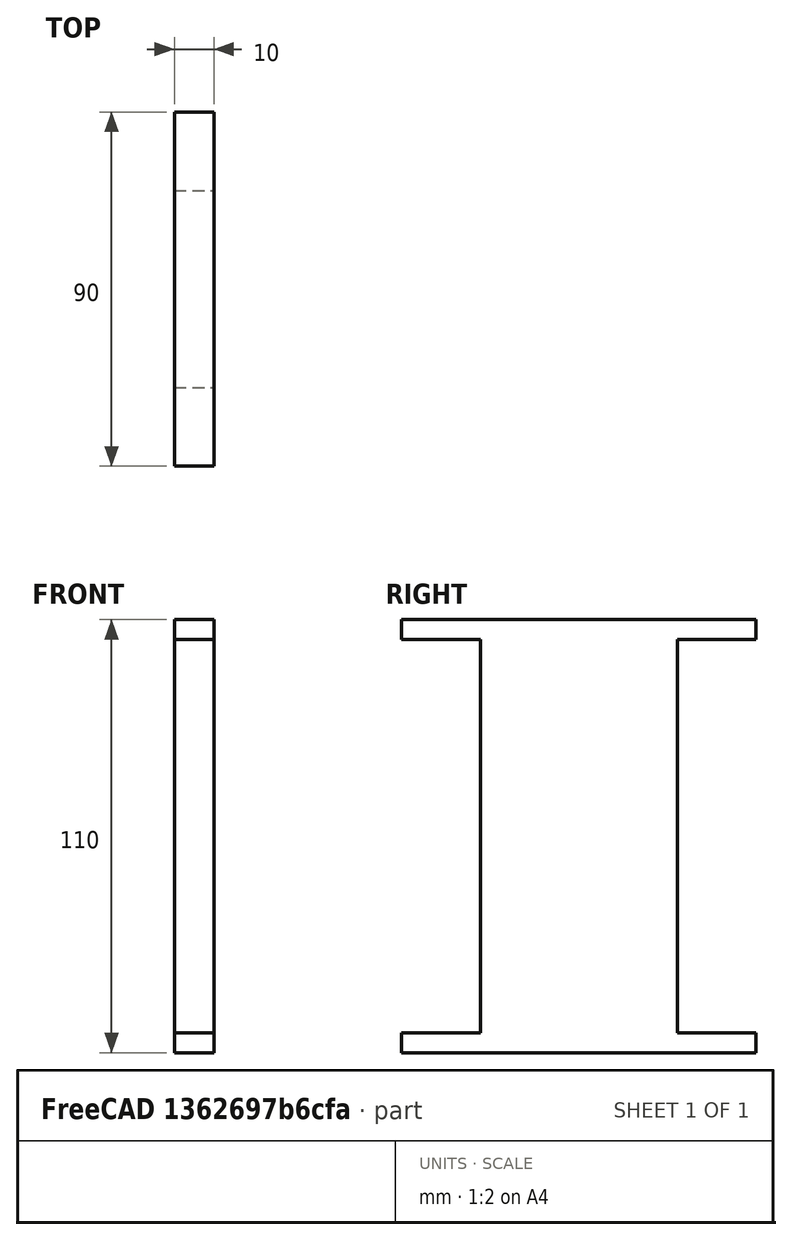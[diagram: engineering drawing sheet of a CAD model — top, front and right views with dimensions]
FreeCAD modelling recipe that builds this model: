
FCSTD DOCUMENT  (FreeCAD 0.20R29603 (Git))
Label: ws
License: All rights reserved
LicenseURL: http://en.wikipedia.org/wiki/All_rights_reserved
objects: Sketcher::SketchObject×1, PartDesign::Pad×1, PartDesign::Body×1
note: 4 computed .brp shape members not serialized (recipe doc carries the construction recipe); baked Part::Feature solids carry a one-line shape summary decoded from their .brp

FEATURE [Sketcher::SketchObject] Sketch
  FullyConstrained = true
  MapMode = 5
  Placement = pos=(0,0,0) rot=(0.57735,0.57735,0.57735;2.0944rad)
  Support = -> [YZ_Plane]
  sketch-geometry (12):
    g0: LineSegment StartX=-45 StartY=55 StartZ=0 EndX=45 EndY=55 EndZ=0
    g1: LineSegment StartX=45 StartY=55 StartZ=0 EndX=45 EndY=50 EndZ=0
    g2: LineSegment StartX=45 StartY=50 StartZ=0 EndX=25 EndY=50 EndZ=0
    g3: LineSegment StartX=25 StartY=50 StartZ=0 EndX=25 EndY=-50 EndZ=0
    g4: LineSegment StartX=25 StartY=-50 StartZ=0 EndX=45 EndY=-50 EndZ=0
    g5: LineSegment StartX=45 StartY=-50 StartZ=0 EndX=45 EndY=-55 EndZ=0
    g6: LineSegment StartX=45 StartY=-55 StartZ=0 EndX=-45 EndY=-55 EndZ=0
    g7: LineSegment StartX=-45 StartY=-55 StartZ=0 EndX=-45 EndY=-50 EndZ=0
    g8: LineSegment StartX=-45 StartY=-50 StartZ=0 EndX=-25 EndY=-50 EndZ=0
    g9: LineSegment StartX=-25 StartY=-50 StartZ=0 EndX=-25 EndY=50 EndZ=0
    g10: LineSegment StartX=-25 StartY=50 StartZ=0 EndX=-45 EndY=50 EndZ=0
    g11: LineSegment StartX=-45 StartY=50 StartZ=0 EndX=-45 EndY=55 EndZ=0
  constraints (34):
    c: Coincident(g0,g1)
    c: Vertical(g1)
    c: Coincident(g1,g2)
    c: Horizontal(g2)
    c: Coincident(g2,g3)
    c: Coincident(g3,g4)
    c: Horizontal(g4)
    c: Coincident(g4,g5)
    c: Vertical(g5)
    c: Coincident(g5,g6)
    c: Horizontal(g6)
    c: Coincident(g6,g7)
    c: Vertical(g7)
    c: Coincident(g7,g8)
    c: Horizontal(g8)
    c: Coincident(g8,g9)
    c: Vertical(g9)
    c: Coincident(g9,g10)
    c: Horizontal(g10)
    c: Coincident(g10,g11)
    c: Coincident(g11,g0)
    c: Vertical(g11)
    c: DistanceX(g0,g0) = 90
    c: DistanceY(g5,g0) = 110
    c: DistanceY(g10,g0) = 5
    c: Symmetric(g0,g0,g-2)
    c: Symmetric(g2,g3,g-1)
    c: Equal(g11,g1)
    c: Equal(g1,g5)
    c: Equal(g5,g7)
    c: DistanceX(g10,g9) = 20
    c: Equal(g10,g2)
    c: Equal(g2,g4)
    c: Equal(g8,g10)
FEATURE [PartDesign::Pad] Pad
  Direction = (1,-2e-16,3e-16)
  Length = 10
  Length2 = 10
  Midplane = true
  Placement = pos=(0,0,0) rot=(0.57735,0.57735,0.57735;2.0944rad)
  Profile = -> Sketch
  ReferenceAxis = -> Sketch [N_Axis]
  Type = 0
FEATURE [PartDesign::Body] Body
  Group = -> [Sketch,Pad]
  Origin = -> Origin
  Tip = -> Pad
